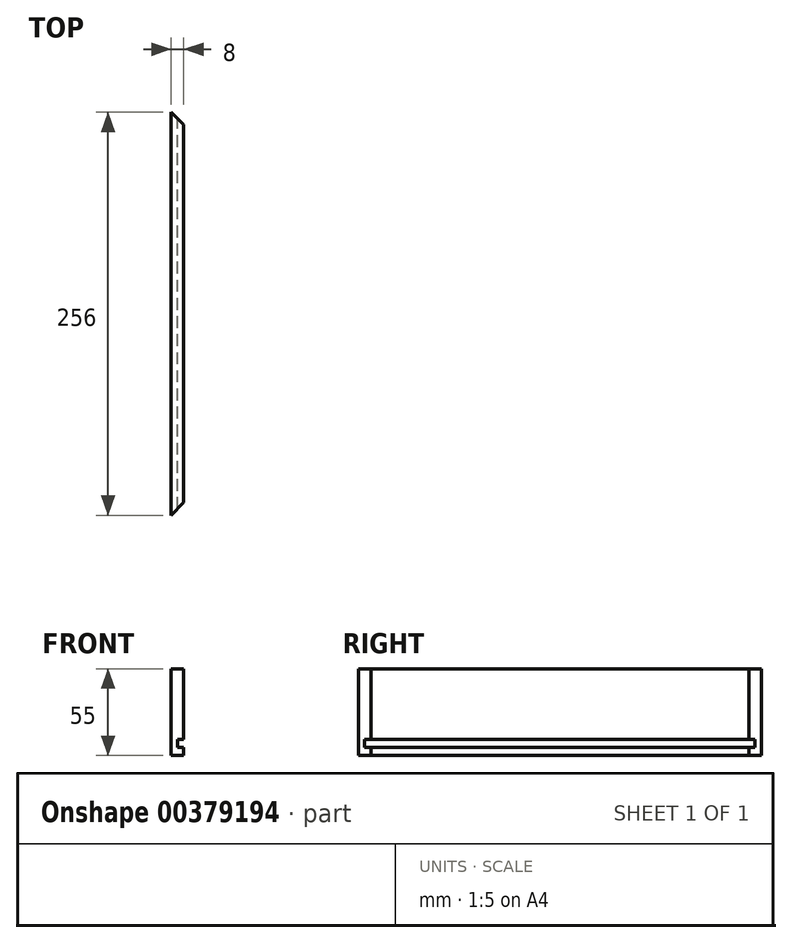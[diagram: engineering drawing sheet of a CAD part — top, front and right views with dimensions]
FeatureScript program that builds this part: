
annotation { "Feature Type Name" : "Feature", "Feature Type Description" : "" }
export const myFeature = defineFeature(function(context is Context, id is Id, definition is map)
    precondition{}
    {
        {
            var Q0;
            Q0=qCreatedBy(makeId("Top.planeOp"),FACE);
            var sketch = newSketch(context, id + "F0", { "sketchPlane" : qUnion([Q0])});
            skLineSegment(sketch, "E0.left", {"start": v(-4, 128) * mm, "end": v(-4, -128) * mm});
            skLineSegment(sketch, "E1", {"start": v(-4, 128) * mm, "end": v(4, 120) * mm});
            skLineSegment(sketch, "E2", {"start": v(-4, -128) * mm, "end": v(4, -120) * mm});
            skLineSegment(sketch, "E3", {"start": v(4, 120) * mm, "end": v(4, -120) * mm});
            skSolve(sketch);
        }
        {
            var Q0;
            Q0=makeQuery(id+"F0.imprint","IMPRINT",FACE,{"disambiguationData":[TD([[makeQuery(id+"F0.imprint","IMPRINT",EDGE,{"derivedFrom":sQuery(id+"F0.wireOp",EDGE,"E0.left")}),1.0]])]});
            extrude(context, id + "F1", {"entities" : qUnion([Q0]), "depth" : 55 * mm});
        }
        {
            var Q0;
            Q0=qCreatedBy(makeId("Front.planeOp"),FACE);
            var sketch = newSketch(context, id + "F2", { "sketchPlane" : qUnion([Q0])});
            skLineSegment(sketch, "E4.bottom", {"start": v(0, 10) * mm, "end": v(4, 10) * mm});
            skLineSegment(sketch, "E4.top", {"start": v(0, 5) * mm, "end": v(4, 5) * mm});
            skLineSegment(sketch, "E4.left", {"start": v(0, 10) * mm, "end": v(0, 5) * mm});
            skLineSegment(sketch, "E4.right", {"start": v(4, 10) * mm, "end": v(4, 5) * mm});
            skSolve(sketch);
        }
        {
            var Q0;
            Q0 = qSketchRegion(id + "F2", true);
            extrude(context, id + "F3", {"entities" : qUnion([Q0]), "operationType" : NewBodyOperationType.REMOVE, "endBound" : BoundingType.SYMMETRIC, "depth" : 256 * mm});
        }
    });
